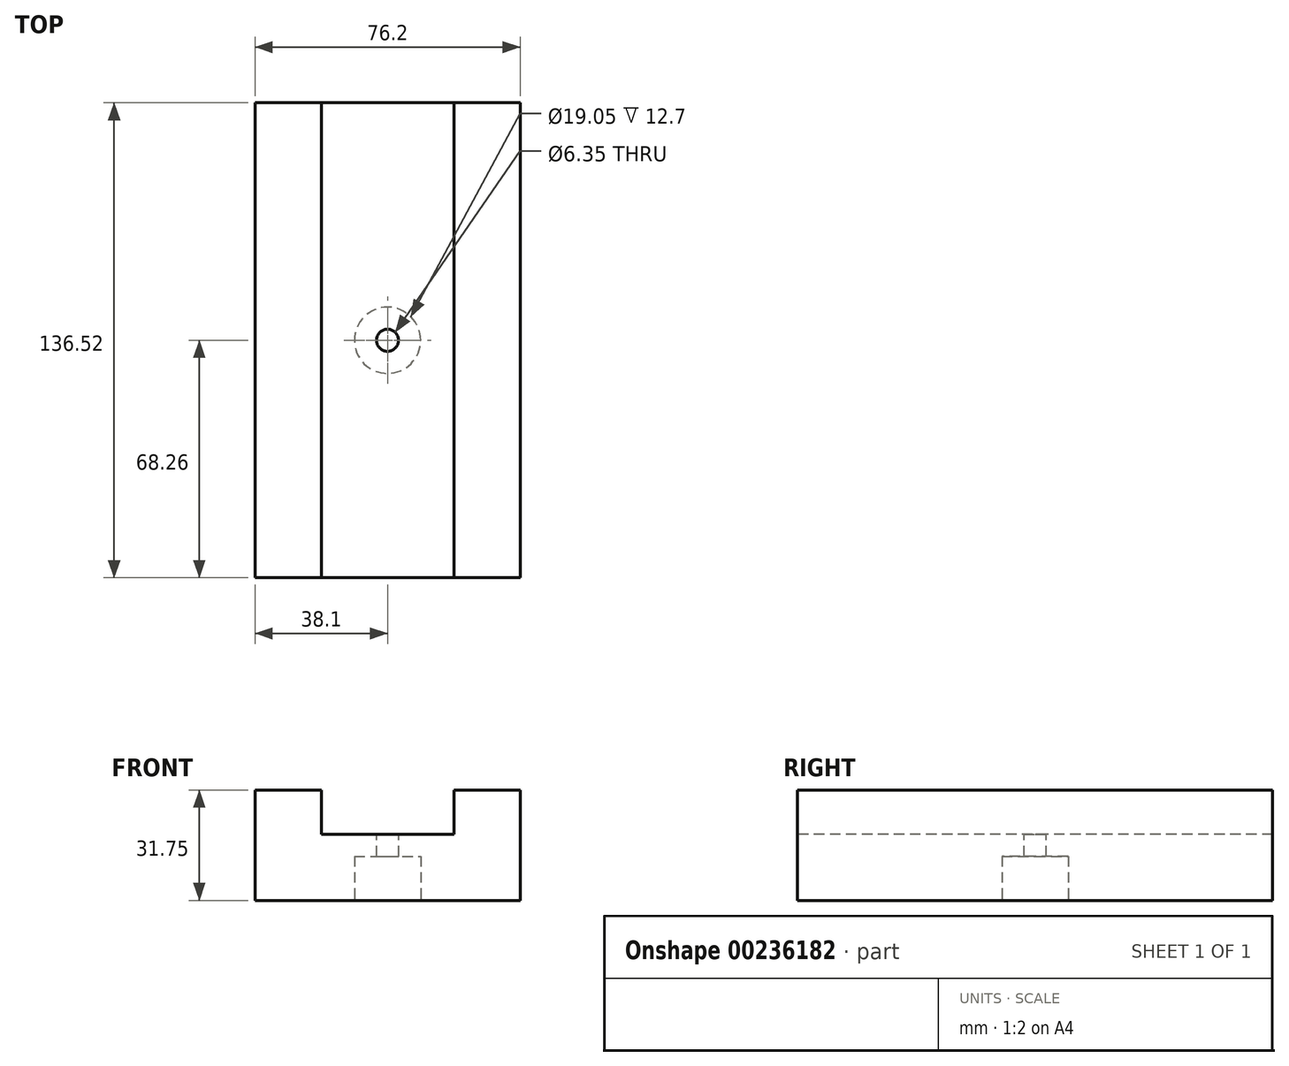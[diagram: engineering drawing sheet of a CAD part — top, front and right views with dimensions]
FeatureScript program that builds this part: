
annotation { "Feature Type Name" : "Feature", "Feature Type Description" : "" }
export const myFeature = defineFeature(function(context is Context, id is Id, definition is map)
    precondition{}
    {
        {
            var Q0;
            Q0=qCreatedBy(makeId("Top.planeOp"),FACE);
            var sketch = newSketch(context, id + "F0", { "sketchPlane" : qUnion([Q0])});
            skLineSegment(sketch, "E0.bottom", {"start": v(38.1, 68.26) * mm, "end": v(-38.1, 68.26) * mm});
            skLineSegment(sketch, "E0.top", {"start": v(38.1, -68.26) * mm, "end": v(-38.1, -68.26) * mm});
            skLineSegment(sketch, "E0.left", {"start": v(38.1, 68.26) * mm, "end": v(38.1, -68.26) * mm});
            skLineSegment(sketch, "E0.right", {"start": v(-38.1, 68.26) * mm, "end": v(-38.1, -68.26) * mm});
            skPoint(sketch, "E0.middle", {"position": v(0, 0) * mm});
            skSolve(sketch);
        }
        {
            var Q0;
            Q0=makeQuery(id+"F0.imprint","IMPRINT",FACE,{"disambiguationData":[TD([[makeQuery(id+"F0.imprint","IMPRINT",EDGE,{"derivedFrom":sQuery(id+"F0.wireOp",EDGE,"E0.bottom")}),1.0]])]});
            extrude(context, id + "F1", {"entities" : qUnion([Q0]), "depth" : 31.75 * mm});
        }
        {
            var Q0;
            Q0=makeQuery(id+"F1.opExtrude","CAP_FACE",FACE,{"disambiguationData":[OSD([sQuery(id+"F0.wireOp",EDGE,"E0.bottom"),sQuery(id+"F0.wireOp",EDGE,"E0.top"),sQuery(id+"F0.wireOp",EDGE,"E0.left"),sQuery(id+"F0.wireOp",EDGE,"E0.right")])],"isStart":false});
            var sketch = newSketch(context, id + "F2", { "sketchPlane" : qUnion([Q0])});
            skLineSegment(sketch, "E1", {"start": v(-38.1, 68.26) * mm, "end": v(-19.05, 68.26) * mm});
            skLineSegment(sketch, "E2", {"start": v(-19.05, 68.26) * mm, "end": v(-19.05, -68.26) * mm});
            skLineSegment(sketch, "E3", {"start": v(-19.05, -68.26) * mm, "end": v(-38.1, -68.26) * mm});
            skLineSegment(sketch, "E4", {"start": v(-38.1, -68.26) * mm, "end": v(-38.1, 68.26) * mm});
            skLineSegment(sketch, "E5", {"start": v(38.1, 68.26) * mm, "end": v(19.05, 68.26) * mm});
            skLineSegment(sketch, "E6", {"start": v(19.05, 68.26) * mm, "end": v(19.05, -68.26) * mm});
            skLineSegment(sketch, "E7", {"start": v(19.05, -68.26) * mm, "end": v(38.1, -68.26) * mm});
            skLineSegment(sketch, "E8", {"start": v(38.1, -68.26) * mm, "end": v(38.1, 68.26) * mm});
            skSolve(sketch);
        }
        {
            var Q0;
            {var subQ0=sQuery(id+"F2.wireOp",EDGE,"E2");Q0=makeQuery(id+"F2.imprint","IMPRINT",FACE,{"disambiguationData":[TD([[makeQuery(id+"F2.imprint","IMPRINT",EDGE,{"derivedFrom":subQ0}),1.0]])]});}
            extrude(context, id + "F3", {"entities" : qUnion([Q0]), "operationType" : NewBodyOperationType.REMOVE, "oppositeDirection" : true, "depth" : 12.7 * mm});
        }
        {
            var Q0;
            Q0=makeQuery(id+"F3.boolean.opBoolean","COPY",FACE,{"derivedFrom":makeQuery(id+"F3.opExtrude","CAP_FACE",FACE,{"disambiguationData":[OSD([sQuery(id+"F0.wireOp",EDGE,"E0.bottom"),sQuery(id+"F0.wireOp",EDGE,"E0.top"),sQuery(id+"F2.wireOp",EDGE,"E2"),sQuery(id+"F2.wireOp",EDGE,"E6")])],"isStart":false})});
            var sketch = newSketch(context, id + "F4", { "sketchPlane" : qUnion([Q0])});
            skCircle(sketch, "E9", {"center": v(0, 0) * mm, "radius": 3.18 * mm});
            skSolve(sketch);
        }
        {
            var Q0;
            Q0=makeQuery(id+"F1.opExtrude","CAP_FACE",FACE,{"disambiguationData":[OSD([sQuery(id+"F0.wireOp",EDGE,"E0.bottom"),sQuery(id+"F0.wireOp",EDGE,"E0.top"),sQuery(id+"F0.wireOp",EDGE,"E0.left"),sQuery(id+"F0.wireOp",EDGE,"E0.right")])],"isStart":true});
            var sketch = newSketch(context, id + "F5", { "sketchPlane" : qUnion([Q0])});
            skCircle(sketch, "E10", {"center": v(0, 0) * mm, "radius": 9.53 * mm});
            skSolve(sketch);
        }
        {
            var Q0;
            Q0=makeQuery(id+"F5.imprint","IMPRINT",FACE,{"disambiguationData":[TD([[makeQuery(id+"F5.imprint","IMPRINT",EDGE,{"derivedFrom":sQuery(id+"F5.wireOp",EDGE,"E10")}),1.0]])]});
            extrude(context, id + "F6", {"entities" : qUnion([Q0]), "operationType" : NewBodyOperationType.REMOVE, "oppositeDirection" : true, "depth" : 12.7 * mm});
        }
        {
            var Q0;
            Q0=makeQuery(id+"F4.imprint","IMPRINT",FACE,{"disambiguationData":[TD([[makeQuery(id+"F4.imprint","IMPRINT",EDGE,{"derivedFrom":sQuery(id+"F4.wireOp",EDGE,"E9")}),1.0]])]});
            extrude(context, id + "F7", {"entities" : qUnion([Q0]), "operationType" : NewBodyOperationType.REMOVE, "oppositeDirection" : true, "depth" : 254 * mm});
        }
    });
